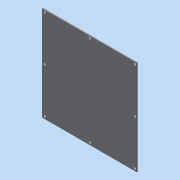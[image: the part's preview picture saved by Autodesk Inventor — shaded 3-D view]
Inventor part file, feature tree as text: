
AUTODESK INVENTOR PART (.ipt)
format: ipt  version: 2015 (Build 190159000, 159)  size: 112,128 bytes
history: native  units: in
note: dims shown in document units (in); Inventor stores cm internally (conversion verified against a paired STEP export)
features: sketch x4, hole x3, extrude x1
ambient origin geometry x8: Origin, YZ Plane, XZ Plane, XY Plane, X Axis, Y Axis, Z Axis, Center Point
bodies: Solid1 (feature_tree)
feature tree (8):
  extrude  "Extrusion1"  Depth=11.811in
  hole  "Hole1"  [1 undecoded]
  hole  "Hole2"  [1 undecoded]
  hole  "Hole3"  [1 undecoded]
  sketch  "Sketch1"  dims[d0=11.811in d1=11.811in]
  sketch  "Sketch2"  dims[d2=0.125in d3=0.0in d4=0.2756in]
  sketch  "Sketch3"  dims[d5=0.2756in d6=0.2756in]
  sketch  "Sketch4"  dims[d7=0.2756in d8=0.2756in d9=0.2756in d10=0.2756in d11=0.2756in d12=0.315in d13=0.75in d14=0.375in d15=0.25in d16=0.5635in d17=1.0in d18=0.8108in d19=8.189in d20=8.189in d21=8.189in d22=1.811in d23=1.811in d24=1.811in d25=8.189in d26=1.811in d27=0.1181in d28=0.75in d29=0.375in d30=0.25in d31=0.5635in d32=1.0in d33=0.8108in d34=5.9055in d35=0.2756in d36=0.2756in d37=5.9055in d38=0.2756in d39=0.2756in d40=5.9055in d41=5.9055in d42=0.315in d43=0.75in d44=0.375in d45=0.25in d46=0.5635in d47=1.0in d48=0.8108in]
note: 3 required parameter values undecoded (feature->parameter linkage not recoverable at this tier; creation-order binding heuristic only, values carry confidence <= 0.55)
